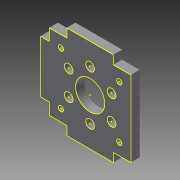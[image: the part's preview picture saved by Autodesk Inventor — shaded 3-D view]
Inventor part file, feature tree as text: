
AUTODESK INVENTOR PART (.ipt)
format: ipt  version: 2015 (Build 190159000, 159)  size: 157,696 bytes
history: native  units: mm
features: sketch x2, extrude x1, projected_geometry x1
ambient origin geometry x8: Origin, YZ Plane, XZ Plane, XY Plane, X Axis, Y Axis, Z Axis, Center Point
bodies: Solid1 (feature_tree)
feature tree (4):
  extrude  "Extrusion1"  Depth=22.0mm
  sketch  "Sketch3"  dims[d3=3.0mm d4=60.0mm d6=360.0deg d8=10.0mm d9=28.0mm d10=32.0mm d11=3.0mm d12=3.0mm d13=3.0mm d14=3.0mm d16=50.0mm d17=3.0mm d18=0.0mm d19=6.0mm d20=3.0mm d21=4.0mm d22=1.8mm d23=4.0mm d24=4.0mm d25=1.8mm d26=4.0mm d27=1.8mm d28=4.0mm d29=1.8mm]
  sketch  "Sketch1"  dims[d0=22.0mm d1=17.0mm]
  projected_geometry  "Projected Loop1"
